# Revit family: Haworth_Epure_DoubleBench_FixedLegs_AP_PRELIMINARY
name_source: partatom
category: Furniture
units: mm (PartAtom-declared; Revit-internal decimal feet)

## family parameters
Always vertical = Yes
Cut with Voids When Loaded = No
OmniClass Number = 23.40.70.14.64.11
OmniClass Title = Office Furniture
Room Calculation Point = No
Shared = No
Work Plane-Based = No

## types (6) — shared parameters
Actual Height = 730 mm  [stored 2.39501 ft]
Assembly Code = E2020200
Cable Tray Finish = Haworth _ Polymer _ Undecided
Description = Haworth - Epure - Double Bench - Fixed Legs
Flip Top Finish = Haworth _ Paint _ Metallic Silver
Leg Height = 695 mm  [stored 2.28018 ft]
Manufacturer = Haworth
Model = SYEPDBF1XXX
No Accessory Kit = No
Revision Number = 1
Size = Verify Final Dim.w/ Haworth
Top Gap Depth = 30 mm  [stored 0.0984252 ft]
Trim Finish = Haworth _ Metal _ Structured White EC
URL = https://www.haworth.com
URL - Product = https://www.haworth.com
Warranty = http://www.haworth.com
Worksurface Depth = 1200, 1400, 1500, 1600 mm
Worksurface Width = 1200, 1400, 1500, 1600, 1800 mm

## per-type parameters (varying)
- 1800 x 1600: Accessory Kit=Yes; Actual Depth=1600 mm  [stored 5.24934 ft]; Actual Width=1800 mm  [stored 5.90551 ft]; Aluminium C L=No; Aluminium C R=No; Aluminium L1=No; Aluminium L2=No; Aluminium Legs=No; Aluminium R1=No; Aluminium R2=No; Cable Tray Double=No; Cable Tray Width=1100 mm  [stored 3.60892 ft]; Depth=800 mm  [stored 2.62467 ft]; End Frame=Yes; End Frame A 1=No; End Frame A 2=No; End Frame W 1=Yes; End Frame W 2=Yes; Flip Top Cable Outlet=No; Intermediary Frame=No; Linking Plate=No; No Cable Tray=Yes; Round Cable Outlet=Yes; Single Cable Tray=No; Start Frame=No; Umbilical Cord=No; Wooden C L=Yes; Wooden C R=No; Wooden L1=No; Wooden L2=No; Wooden Legs=Yes; Wooden R1=No; Wooden R2=No; with Screen Gap=No; without Screen Gap=Yes
- 1200 x 1200: Accessory Kit=No; Actual Depth=1200 mm; Actual Width=1200 mm; Aluminium C L=No; Aluminium C R=Yes; Aluminium L1=Yes; Aluminium L2=Yes; Aluminium Legs=Yes; Aluminium R1=Yes; Aluminium R2=Yes; Cable Tray Double=No; Cable Tray Width=500 mm  [stored 1.64042 ft]; Depth=600 mm; End Frame=No; End Frame A 1=No; End Frame A 2=No; End Frame W 1=No; End Frame W 2=No; Flip Top Cable Outlet=No; Intermediary Frame=No; Linking Plate=Yes; No Cable Tray=No; Round Cable Outlet=No; Single Cable Tray=Yes; Start Frame=Yes; Umbilical Cord=No; Wooden C L=No; Wooden C R=No; Wooden L1=No; Wooden L2=No; Wooden Legs=No; Wooden R1=No; Wooden R2=No; with Screen Gap=No; without Screen Gap=Yes
- 1500 x 1400: Accessory Kit=No; Actual Depth=1400 mm; Actual Width=1500 mm  [stored 4.92126 ft]; Aluminium C L=No; Aluminium C R=No; Aluminium L1=No; Aluminium L2=No; Aluminium Legs=No; Aluminium R1=No; Aluminium R2=No; Cable Tray Double=No; Cable Tray Width=800 mm  [stored 2.62467 ft]; Depth=700 mm; End Frame=No; End Frame A 1=No; End Frame A 2=No; End Frame W 1=No; End Frame W 2=No; Flip Top Cable Outlet=No; Intermediary Frame=No; Linking Plate=Yes; No Cable Tray=No; Round Cable Outlet=No; Single Cable Tray=Yes; Start Frame=Yes; Umbilical Cord=No; Wooden C L=No; Wooden C R=Yes; Wooden L1=Yes; Wooden L2=Yes; Wooden Legs=Yes; Wooden R1=Yes; Wooden R2=Yes; with Screen Gap=No; without Screen Gap=Yes
- 1400 x 1500: Accessory Kit=Yes; Actual Depth=1500 mm  [stored 4.92126 ft]; Actual Width=1400 mm; Aluminium C L=No; Aluminium C R=No; Aluminium L1=No; Aluminium L2=No; Aluminium Legs=No; Aluminium R1=No; Aluminium R2=No; Cable Tray Double=Yes; Cable Tray Width=700 mm; Depth=735 mm; End Frame=No; End Frame A 1=No; End Frame A 2=No; End Frame W 1=No; End Frame W 2=No; Flip Top Cable Outlet=Yes; Intermediary Frame=Yes; Linking Plate=Yes; No Cable Tray=No; Round Cable Outlet=No; Single Cable Tray=No; Start Frame=No; Umbilical Cord=No; Wooden C L=Yes; Wooden C R=Yes; Wooden L1=No; Wooden L2=No; Wooden Legs=Yes; Wooden R1=Yes; Wooden R2=Yes; with Screen Gap=Yes; without Screen Gap=No
- 1600 x 1500: Accessory Kit=Yes; Actual Depth=1500 mm  [stored 4.92126 ft]; Actual Width=1600 mm  [stored 5.24934 ft]; Aluminium C L=Yes; Aluminium C R=Yes; Aluminium L1=No; Aluminium L2=No; Aluminium Legs=Yes; Aluminium R1=No; Aluminium R2=No; Cable Tray Double=Yes; Cable Tray Width=900 mm  [stored 2.95276 ft]; Depth=735 mm; End Frame=No; End Frame A 1=No; End Frame A 2=No; End Frame W 1=No; End Frame W 2=No; Flip Top Cable Outlet=Yes; Intermediary Frame=Yes; Linking Plate=Yes; No Cable Tray=No; Round Cable Outlet=No; Single Cable Tray=No; Start Frame=No; Umbilical Cord=Yes; Wooden C L=No; Wooden C R=No; Wooden L1=No; Wooden L2=No; Wooden Legs=No; Wooden R1=No; Wooden R2=No; with Screen Gap=Yes; without Screen Gap=No
- 1400 x 1600: Accessory Kit=Yes; Actual Depth=1600 mm  [stored 5.24934 ft]; Actual Width=1400 mm; Aluminium C L=Yes; Aluminium C R=No; Aluminium L1=No; Aluminium L2=No; Aluminium Legs=Yes; Aluminium R1=No; Aluminium R2=No; Cable Tray Double=No; Cable Tray Width=700 mm; Depth=800 mm  [stored 2.62467 ft]; End Frame=Yes; End Frame A 1=Yes; End Frame A 2=Yes; End Frame W 1=No; End Frame W 2=No; Flip Top Cable Outlet=No; Intermediary Frame=No; Linking Plate=No; No Cable Tray=Yes; Round Cable Outlet=Yes; Single Cable Tray=No; Start Frame=No; Umbilical Cord=Yes; Wooden C L=No; Wooden C R=No; Wooden L1=No; Wooden L2=No; Wooden Legs=No; Wooden R1=No; Wooden R2=No; with Screen Gap=No; without Screen Gap=Yes

note: [stored X ft] marks values corroborated as IEEE doubles in the binary element streams (Revit-internal decimal feet)

## geometry (parser evidence)
native form markers: Sweep x32
no freeform markers — native parametric forms only
